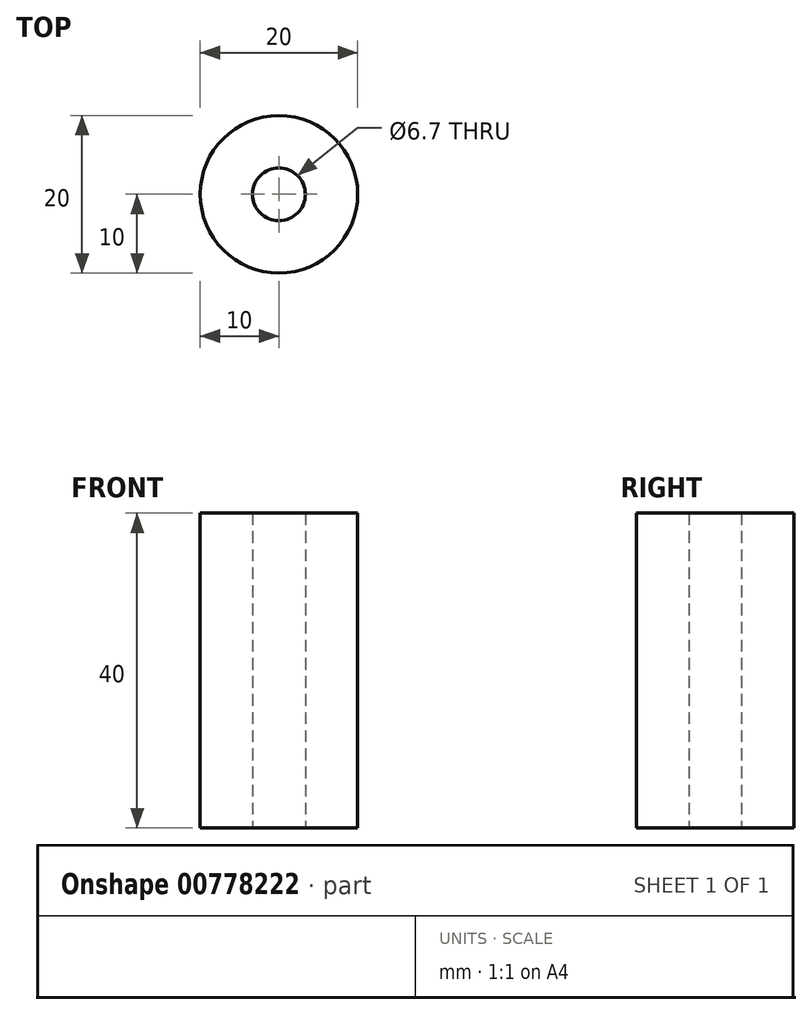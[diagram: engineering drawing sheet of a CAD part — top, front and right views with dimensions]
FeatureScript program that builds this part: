
annotation { "Feature Type Name" : "Feature", "Feature Type Description" : "" }
export const myFeature = defineFeature(function(context is Context, id is Id, definition is map)
    precondition{}
    {
        {
            var Q0;
            Q0=qCreatedBy(makeId("Top.planeOp"),FACE);
            var sketch = newSketch(context, id + "F0", { "sketchPlane" : qUnion([Q0])});
            skCircle(sketch, "E0", {"center": v(0, 0) * mm, "radius": 10 * mm});
            skCircle(sketch, "E1", {"center": v(0, 0) * mm, "radius": 3.35 * mm});
            skSolve(sketch);
        }
        {
            var Q0;
            Q0=makeQuery(id+"F0.imprint","IMPRINT",FACE,{"disambiguationData":[TD([[makeQuery(id+"F0.imprint","IMPRINT",EDGE,{"derivedFrom":sQuery(id+"F0.wireOp",EDGE,"E0")}),1.0]])]});
            extrude(context, id + "F1", {"entities" : qUnion([Q0]), "depth" : 40 * mm, "offsetDistance" : 25.4 * mm});
        }
    });
